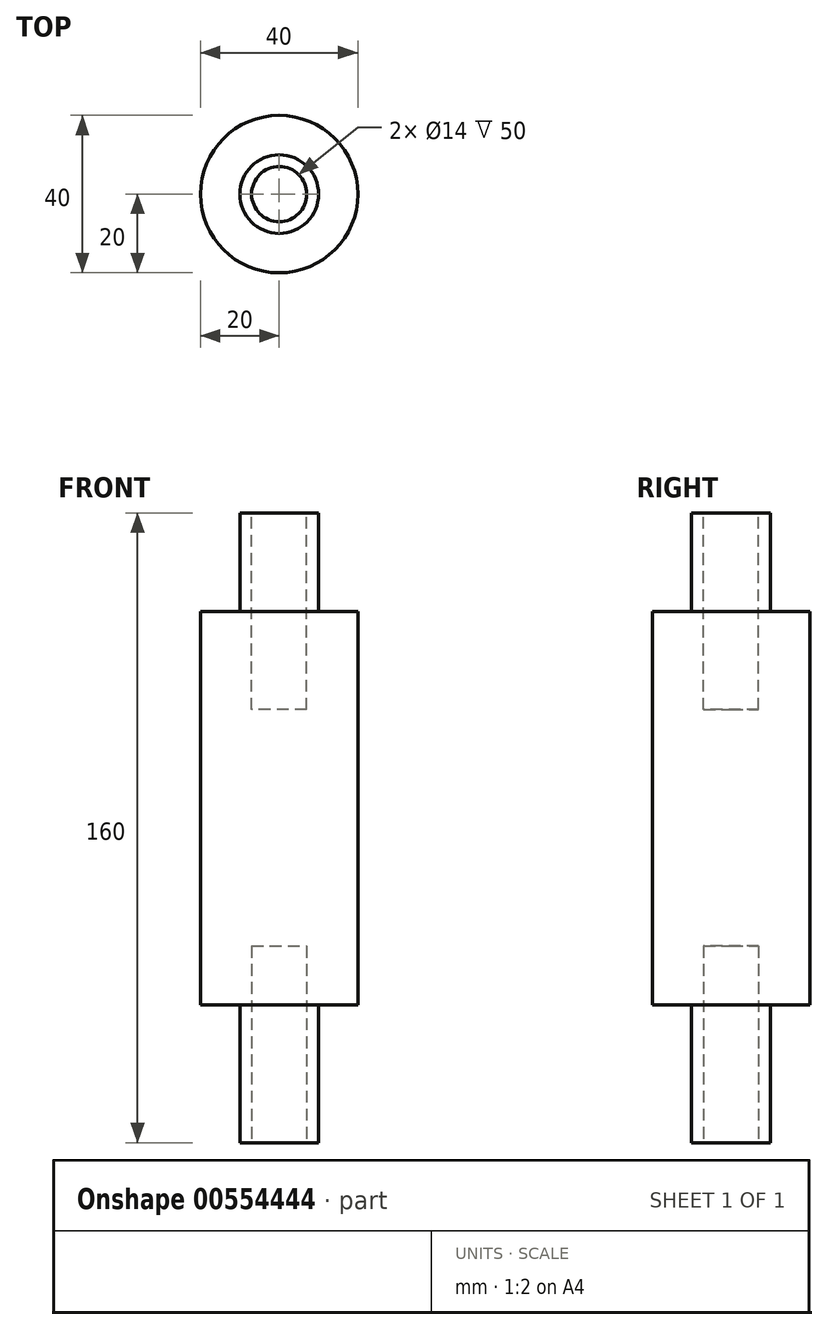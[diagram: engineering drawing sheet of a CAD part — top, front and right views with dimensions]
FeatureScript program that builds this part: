
annotation { "Feature Type Name" : "Feature", "Feature Type Description" : "" }
export const myFeature = defineFeature(function(context is Context, id is Id, definition is map)
    precondition{}
    {
        {
            var Q0;
            Q0=qCreatedBy(makeId("Top.planeOp"),FACE);
            var sketch = newSketch(context, id + "F0", { "sketchPlane" : qUnion([Q0])});
            skCircle(sketch, "E0", {"center": v(0, 0) * mm, "radius": 10 * mm});
            skCircle(sketch, "E1", {"center": v(0, 0) * mm, "radius": 20 * mm});
            skSolve(sketch);
        }
        {
            var Q0;
            Q0=makeQuery(id+"F0.imprint","IMPRINT",FACE,{"disambiguationData":[TD([[makeQuery(id+"F0.imprint","IMPRINT",EDGE,{"derivedFrom":sQuery(id+"F0.wireOp",EDGE,"E0")}),1.0]])]});
            extrude(context, id + "F1", {"entities" : qUnion([Q0]), "oppositeDirection" : true, "depth" : 35 * mm, "offsetDistance" : 25 * mm});
        }
        {
            var Q0;
            Q0 = qSketchRegion(id + "F0", true);
            var Q1;
            Q1=makeQuery(id+"F1.opExtrude","CAP_FACE",FACE,{"disambiguationData":[OSD([sQuery(id+"F0.wireOp",EDGE,"E0")])],"isStart":true});
            extrude(context, id + "F2", {"entities" : qUnion([Q0, Q1]), "operationType" : NewBodyOperationType.ADD, "depth" : 100 * mm, "offsetDistance" : 25 * mm});
        }
        {
            var Q0;
            {var subQ0=sQuery(id+"F0.wireOp",EDGE,"E0");Q0=makeQuery(id+"F2.boolean.opBoolean","MERGE",FACE,{"derivedFrom":[makeQuery(id+"F2.opExtrude","CAP_FACE",FACE,{"disambiguationData":[OSD([subQ0,sQuery(id+"F0.wireOp",EDGE,"E1")])],"isStart":false}),makeQuery(id+"F2.opExtrude","CAP_FACE",FACE,{"disambiguationData":[OSD([subQ0])],"isStart":false})]});}
            var sketch = newSketch(context, id + "F3", { "sketchPlane" : qUnion([Q0])});
            skCircle(sketch, "E2", {"center": v(0, 0) * mm, "radius": 10 * mm});
            skSolve(sketch);
        }
        {
            var Q0;
            Q0 = qSketchRegion(id + "F3", true);
            extrude(context, id + "F4", {"entities" : qUnion([Q0]), "operationType" : NewBodyOperationType.ADD, "depth" : 25 * mm, "offsetDistance" : 25 * mm});
        }
        {
            var Q0;
            Q0=makeQuery(id+"F4.opExtrude","CAP_FACE",FACE,{"disambiguationData":[OSD([sQuery(id+"F3.wireOp",EDGE,"E2")])],"isStart":false});
            var sketch = newSketch(context, id + "F5", { "sketchPlane" : qUnion([Q0])});
            skCircle(sketch, "E3", {"center": v(0, 0) * mm, "radius": 7 * mm});
            skSolve(sketch);
        }
        {
            var Q0;
            Q0 = qSketchRegion(id + "F5", true);
            extrude(context, id + "F6", {"entities" : qUnion([Q0]), "operationType" : NewBodyOperationType.REMOVE, "oppositeDirection" : true, "depth" : 50 * mm, "offsetDistance" : 25 * mm});
        }
        {
            var Q0;
            Q0=makeQuery(id+"F1.opExtrude","CAP_FACE",FACE,{"disambiguationData":[OSD([sQuery(id+"F0.wireOp",EDGE,"E0")])],"isStart":false});
            var sketch = newSketch(context, id + "F7", { "sketchPlane" : qUnion([Q0])});
            skCircle(sketch, "E4", {"center": v(0, 0) * mm, "radius": 7 * mm});
            skSolve(sketch);
        }
        {
            var Q0;
            Q0 = qSketchRegion(id + "F7", true);
            extrude(context, id + "F8", {"entities" : qUnion([Q0]), "operationType" : NewBodyOperationType.REMOVE, "oppositeDirection" : true, "depth" : 50 * mm, "offsetDistance" : 25 * mm});
        }
    });
